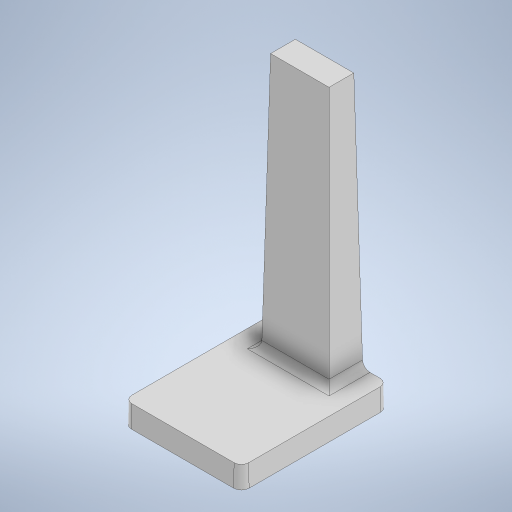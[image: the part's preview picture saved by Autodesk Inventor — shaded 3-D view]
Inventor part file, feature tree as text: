
AUTODESK INVENTOR PART (.ipt)
format: ipt  version: 2023 (Build 270158000, 158)  size: 268,800 bytes
history: native  units: in
note: dims shown in document units (in); Inventor stores cm internally (conversion verified against a paired STEP export)
features: extrude x2, fillet x2, draft x2, sketch x1
ambient origin geometry x8: Origin, YZ Plane, XZ Plane, XY Plane, X Axis, Y Axis, Z Axis, Center Point
bodies: Solid1 (feature_tree)
feature tree (7):
  sketch  "Sketch1"  dims[d0=4.375in d1=0.5in d2=4.75in d3=2.5in d4=1.0in d5=0.0in d24=1.5in d25=0.5in d26=0.0in d27=0.0in d29=0.125in d30=0.0069in d31=0.0069in d32=0.125in]
  extrude  "Extrusion1"  Depth=0.5in
  extrude  "Extrusion3"  Depth=4.75in
  fillet  "Fillet2"  Radius=2.5in
  draft  "FaceDraft1"
  draft  "FaceDraft2"
  fillet  "Fillet3"  Radius=1.0in
